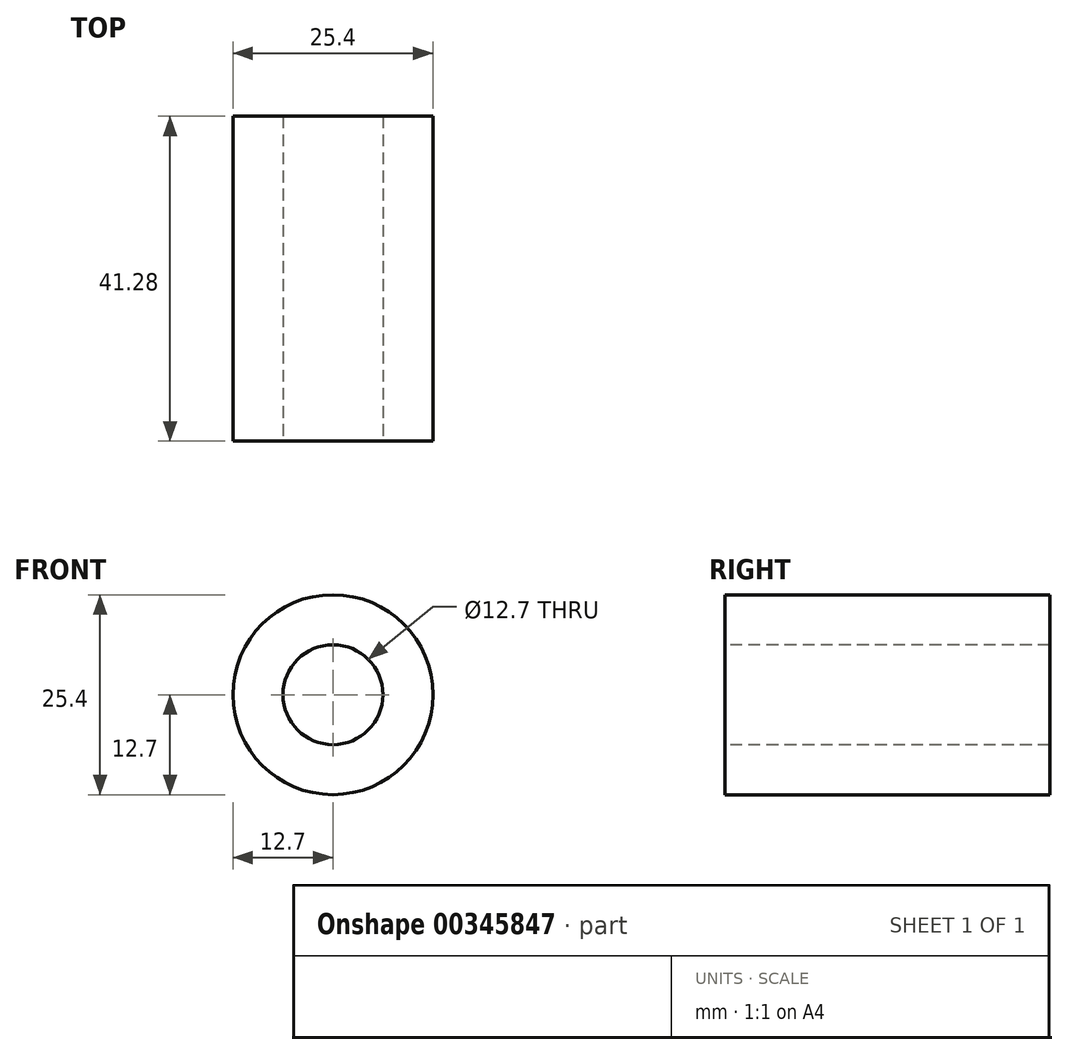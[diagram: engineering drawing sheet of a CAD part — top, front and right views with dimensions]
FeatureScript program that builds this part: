
annotation { "Feature Type Name" : "Feature", "Feature Type Description" : "" }
export const myFeature = defineFeature(function(context is Context, id is Id, definition is map)
    precondition{}
    {
        {
            var Q0;
            Q0=qCreatedBy(makeId("Front.planeOp"),FACE);
            var sketch = newSketch(context, id + "F1", { "sketchPlane" : qUnion([Q0])});
            skCircle(sketch, "E0", {"center": v(0, 0) * mm, "radius": 12.7 * mm});
            skCircle(sketch, "E1", {"center": v(0, 0) * mm, "radius": 6.35 * mm});
            skSolve(sketch);
        }
        {
            var Q0;
            Q0=makeQuery(id+"F1.imprint","IMPRINT",FACE,{"disambiguationData":[TD([[makeQuery(id+"F1.imprint","IMPRINT",EDGE,{"derivedFrom":sQuery(id+"F1.wireOp",EDGE,"E0")}),1.0]])]});
            extrude(context, id + "F0", {"entities" : qUnion([Q0]), "oppositeDirection" : true, "depth" : 41.27 * mm});
        }
    });
